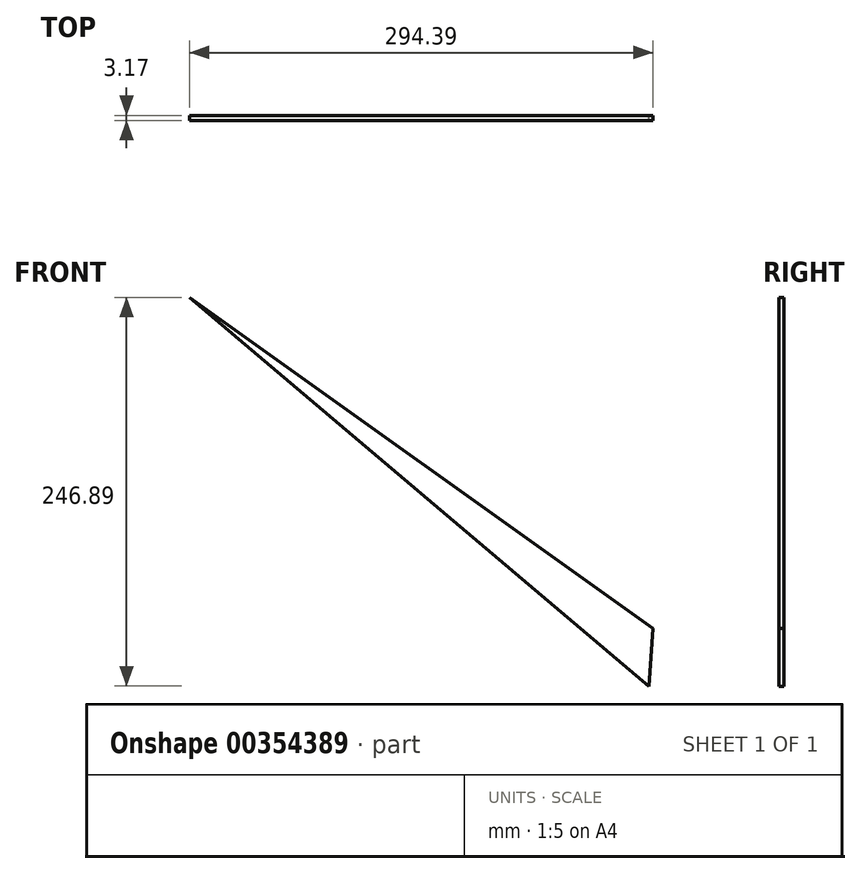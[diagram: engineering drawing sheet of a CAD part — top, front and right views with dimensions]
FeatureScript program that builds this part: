
annotation { "Feature Type Name" : "Feature", "Feature Type Description" : "" }
export const myFeature = defineFeature(function(context is Context, id is Id, definition is map)
    precondition{}
    {
        {
            var Q0;
            Q0=qCreatedBy(makeId("Front.planeOp"),FACE);
            var sketch = newSketch(context, id + "F0", { "sketchPlane" : qUnion([Q0])});
            skLineSegment(sketch, "E0", {"start": v(0, 0) * mm, "end": v(-294.4, 210.13) * mm});
            skLineSegment(sketch, "E1", {"start": v(-294.4, 210.13) * mm, "end": v(-2.55, -36.76) * mm});
            skLineSegment(sketch, "E2", {"start": v(-2.55, -36.76) * mm, "end": v(0, 0) * mm});
            skSolve(sketch);
        }
        {
            var Q0;
            Q0 = qSketchRegion(id + "F0", true);
            extrude(context, id + "F1", {"entities" : qUnion([Q0]), "depth" : 3.17 * mm});
        }
    });
